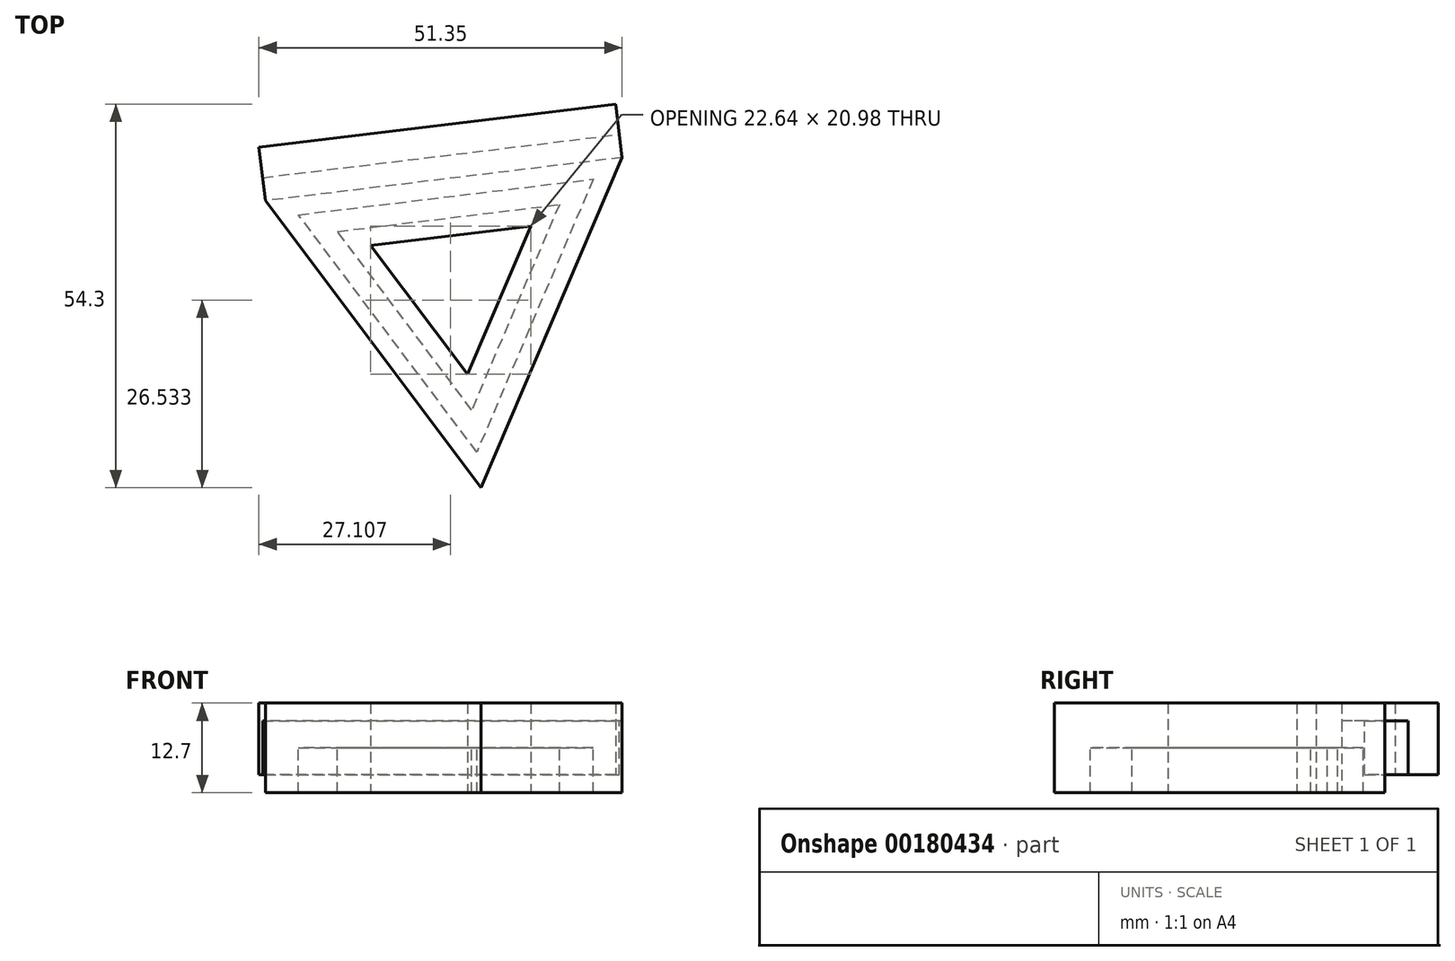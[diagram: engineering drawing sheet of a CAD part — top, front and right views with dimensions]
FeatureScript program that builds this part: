
annotation { "Feature Type Name" : "Feature", "Feature Type Description" : "" }
export const myFeature = defineFeature(function(context is Context, id is Id, definition is map)
    precondition{}
    {
        {
            var Q0;
            Q0=qCreatedBy(makeId("Top.planeOp"),FACE);
            var sketch = newSketch(context, id + "F0", { "sketchPlane" : qUnion([Q0])});
            skCircle(sketch, "E0.cCircle", {"center": v(-13.5, 9.85) * mm, "radius": 14.66 * mm, "construction": true});
            skLineSegment(sketch, "E0.0", {"start": v(9.96, 27.47) * mm, "end": v(-9.96, -19.26) * mm});
            skLineSegment(sketch, "E0.1", {"start": v(-9.96, -19.26) * mm, "end": v(-40.47, 21.35) * mm});
            skLineSegment(sketch, "E0.2", {"start": v(-40.47, 21.35) * mm, "end": v(9.96, 27.47) * mm});
            skPoint(sketch, "E0.0.midPoint", {"position": v(0, 4.1) * mm});
            skLineSegment(sketch, "E1.0", {"start": v(-35.8, 19.36) * mm, "end": v(5.9, 24.42) * mm});
            skLineSegment(sketch, "E1.1", {"start": v(-10.57, -14.22) * mm, "end": v(-35.8, 19.36) * mm});
            skLineSegment(sketch, "E1.2", {"start": v(5.9, 24.42) * mm, "end": v(-10.57, -14.22) * mm});
            skLineSegment(sketch, "E2.0", {"start": v(-30.28, 17.01) * mm, "end": v(1.1, 20.82) * mm});
            skLineSegment(sketch, "E2.1", {"start": v(-11.3, -8.26) * mm, "end": v(-30.28, 17.01) * mm});
            skLineSegment(sketch, "E2.2", {"start": v(1.1, 20.82) * mm, "end": v(-11.3, -8.26) * mm});
            skLineSegment(sketch, "E3.0", {"start": v(-25.6, 15.02) * mm, "end": v(-2.96, 17.76) * mm});
            skLineSegment(sketch, "E3.1", {"start": v(-11.9, -3.22) * mm, "end": v(-25.6, 15.02) * mm});
            skLineSegment(sketch, "E3.2", {"start": v(-2.96, 17.76) * mm, "end": v(-11.9, -3.22) * mm});
            skSolve(sketch);
        }
        {
            var Q0;
            Q0=makeQuery(id+"F0.imprint","IMPRINT",FACE,{"disambiguationData":[TD([[makeQuery(id+"F0.imprint","IMPRINT",EDGE,{"derivedFrom":sQuery(id+"F0.wireOp",EDGE,"E0.0")}),-1.0]])]});
            var Q1;
            Q1=makeQuery(id+"F0.imprint","IMPRINT",FACE,{"disambiguationData":[TD([[makeQuery(id+"F0.imprint","IMPRINT",EDGE,{"derivedFrom":sQuery(id+"F0.wireOp",EDGE,"E1.0")}),-1.0]])]});
            var Q2;
            Q2=makeQuery(id+"F0.imprint","IMPRINT",FACE,{"disambiguationData":[TD([[makeQuery(id+"F0.imprint","IMPRINT",EDGE,{"derivedFrom":sQuery(id+"F0.wireOp",EDGE,"E2.0")}),-1.0]])]});
            extrude(context, id + "F1", {"entities" : qUnion([Q0, Q1, Q2]), "depth" : 6.35 * mm});
        }
        {
            var Q0;
            Q0=makeQuery(id+"F0.imprint","IMPRINT",FACE,{"disambiguationData":[TD([[makeQuery(id+"F0.imprint","IMPRINT",EDGE,{"derivedFrom":sQuery(id+"F0.wireOp",EDGE,"E0.0")}),-1.0]])]});
            var Q1;
            Q1=makeQuery(id+"F0.imprint","IMPRINT",FACE,{"disambiguationData":[TD([[makeQuery(id+"F0.imprint","IMPRINT",EDGE,{"derivedFrom":sQuery(id+"F0.wireOp",EDGE,"E2.0")}),-1.0]])]});
            extrude(context, id + "F2", {"entities" : qUnion([Q0, Q1]), "operationType" : NewBodyOperationType.ADD, "oppositeDirection" : true, "depth" : 6.35 * mm});
        }
        {
            var Q0;
            {var subQ0=sQuery(id+"F0.wireOp",EDGE,"E0.2");Q0=makeQuery(id+"F2.boolean.opBoolean","MERGE",FACE,{"derivedFrom":[makeQuery(id+"F1.opExtrude","SWEPT_FACE",FACE,{"disambiguationData":[OSD([subQ0])]}),makeQuery(id+"F2.opExtrude","SWEPT_FACE",FACE,{"disambiguationData":[OSD([subQ0])]})]});}
            var sketch = newSketch(context, id + "F3", { "sketchPlane" : qUnion([Q0])});
            skLineSegment(sketch, "E4.bottom", {"start": v(-13.2, 6.35) * mm, "end": v(37.6, 6.35) * mm});
            skLineSegment(sketch, "E4.top", {"start": v(-13.2, 3.81) * mm, "end": v(37.6, 3.81) * mm});
            skLineSegment(sketch, "E4.left", {"start": v(-13.2, 6.35) * mm, "end": v(-13.2, 3.81) * mm});
            skLineSegment(sketch, "E4.right", {"start": v(37.6, 6.35) * mm, "end": v(37.6, 3.81) * mm});
            skSolve(sketch);
        }
        {
            var Q0;
            Q0 = qSketchRegion(id + "F3", true);
            extrude(context, id + "F4", {"entities" : qUnion([Q0]), "operationType" : NewBodyOperationType.ADD, "depth" : 7.62 * mm});
        }
        {
            var Q0;
            Q0=makeQuery(id+"F4.opExtrude","SWEPT_FACE",FACE,{"disambiguationData":[OSD([sQuery(id+"F3.wireOp",EDGE,"E4.top")])]});
            var sketch = newSketch(context, id + "F5", { "sketchPlane" : qUnion([Q0])});
            skLineSegment(sketch, "E5", {"start": v(-40.47, -21.35) * mm, "end": v(-40.87, -24.63) * mm});
            skLineSegment(sketch, "E6", {"start": v(-40.87, -24.63) * mm, "end": v(9.56, -30.75) * mm});
            skLineSegment(sketch, "E7", {"start": v(9.56, -30.75) * mm, "end": v(9.96, -27.47) * mm});
            skLineSegment(sketch, "E8", {"start": v(9.96, -27.47) * mm, "end": v(-40.47, -21.35) * mm});
            skSolve(sketch);
        }
        {
            var Q0;
            {var subQ0=sQuery(id+"F5.wireOp",EDGE,"E6");Q0=makeQuery(id+"F5.imprint","IMPRINT",FACE,{"disambiguationData":[TD([[makeQuery(id+"F5.imprint","IMPRINT",EDGE,{"derivedFrom":subQ0}),-1.0]])]});}
            extrude(context, id + "F6", {"entities" : qUnion([Q0]), "operationType" : NewBodyOperationType.ADD, "depth" : 7.62 * mm});
        }
    });
